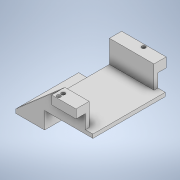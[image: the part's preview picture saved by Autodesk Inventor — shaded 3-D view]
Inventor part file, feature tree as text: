
AUTODESK INVENTOR PART (.ipt)
format: ipt  version: 2020 (Build 240168000, 168)  size: 364,544 bytes
history: native  units: mm
features: sketch x10, extrude x10, projected_geometry x5, hole x2, other x1
ambient origin geometry x8: Origin, YZ Plane, XZ Plane, XY Plane, X Axis, Y Axis, Z Axis, Center Point
bodies: Body1 (feature_tree)
feature tree (28):
  other  "솔리드1"
  sketch  "스케치1"
  extrude  "돌출1"  Depth=50.0mm
  extrude  "돌출2"  Depth=4.134mm
  sketch  "스케치2"
  extrude  "돌출7"  Depth=4.134mm
  extrude  "돌출15"  Depth=4.134mm
  extrude  "돌출11"  Depth=4.134mm
  extrude  "돌출16"  Depth=12.0mm
  hole  "구멍1"  [1 undecoded]
  sketch  "스케치18"
  extrude  "돌출20"  Depth=32.0mm
  extrude  "돌출21"  Depth=15.0mm
  extrude  "돌출23"  Depth=10.0mm TaperAngle=0.0deg
  extrude  "돌출24"  Depth=82.3mm TaperAngle=0.0deg
  hole  "구멍4"  [1 undecoded]
  projected_geometry  "투영된 루프1"
  sketch  "스케치7"
  sketch  "스케치10"
  sketch  "스케치17"
  sketch  "스케치21"
  projected_geometry  "투영된 루프13"
  sketch  "스케치23"
  projected_geometry  "투영된 루프14"
  sketch  "스케치25"
  projected_geometry  "투영된 루프16"
  sketch  "스케치27"
  projected_geometry  "투영된 루프18"
note: 2 required parameter values undecoded (feature->parameter linkage not recoverable at this tier; creation-order binding heuristic only, values carry confidence <= 0.55)
